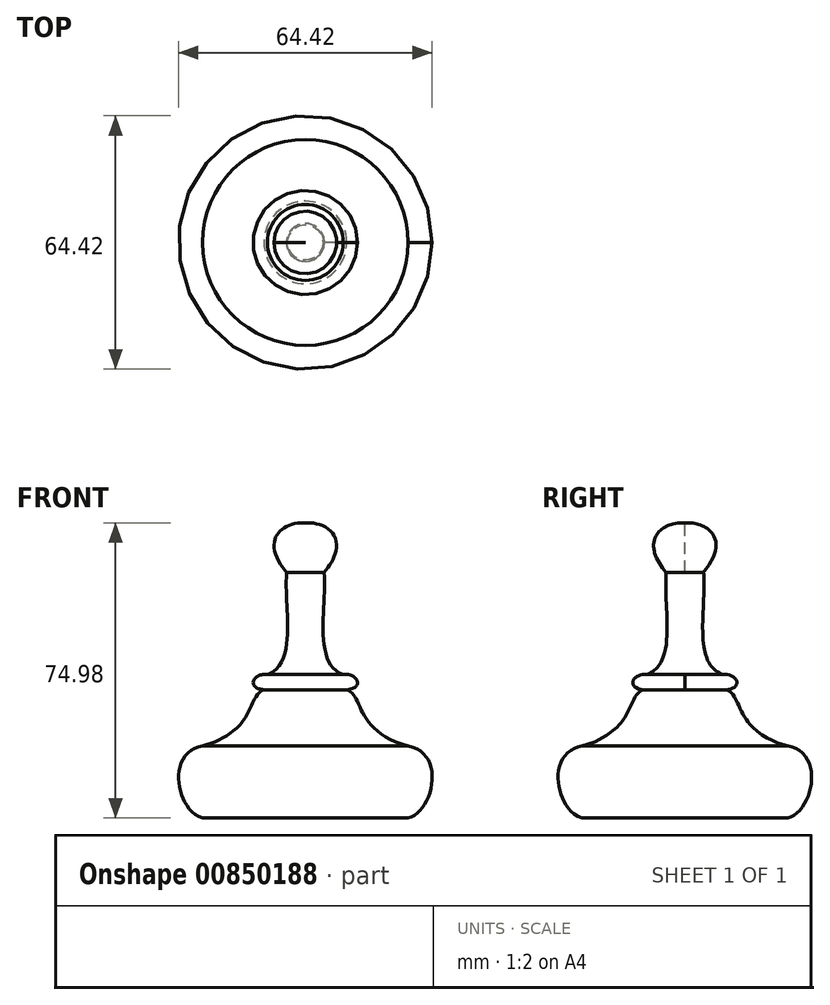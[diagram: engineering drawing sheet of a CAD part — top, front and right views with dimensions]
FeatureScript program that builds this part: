
annotation { "Feature Type Name" : "Feature", "Feature Type Description" : "" }
export const myFeature = defineFeature(function(context is Context, id is Id, definition is map)
    precondition{}
    {
        {
            var Q0;
            Q0=qCreatedBy(makeId("Front.planeOp"),FACE);
            var sketch = newSketch(context, id + "F0", { "sketchPlane" : qUnion([Q0])});
            skLineSegment(sketch, "E0", {"start": v(0, 0) * mm, "end": v(-26.14, 0) * mm});
            skFitSpline(sketch, "E1", {"points": [v(-26.14, 0) * mm, v(-26.14, 18.22) * mm], "startDerivative": vector(-19.1, 4.33) * mm, "endDerivative": vector(28.96, 4.76) * mm});
            skFitSpline(sketch, "E2", {"points": [v(-26.14, 18.22) * mm, v(-10.5, 32.53) * mm], "startDerivative": vector(41.24, 11.2) * mm, "endDerivative": vector(12.9, 3.47) * mm});
            skFitSpline(sketch, "E3", {"points": [v(-10.5, 32.53) * mm, v(-9.63, 36.43) * mm], "startDerivative": vector(-14.13, 1.41) * mm, "endDerivative": vector(10.63, -1.32) * mm});
            skFitSpline(sketch, "E4", {"points": [v(-9.63, 36.43) * mm, v(-4.77, 62.38) * mm], "startDerivative": vector(23.62, 7.74) * mm, "endDerivative": vector(2.22, 25.95) * mm});
            skFitSpline(sketch, "E5", {"points": [v(-4.77, 62.38) * mm, v(0, 74.97) * mm], "startDerivative": vector(-20.62, 24.13) * mm, "endDerivative": vector(18.38, -0.86) * mm});
            skLineSegment(sketch, "E6", {"start": v(0, 74.97) * mm, "end": v(0, 0) * mm});
            skSolve(sketch);
        }
        {
            var Q0;
            Q0 = qSketchRegion(id + "F0", true);
            var Q1;
            Q1=sQuery(id+"F0.wireOp",EDGE,"E6");
            revolve(context, id + "F1", {"surfaceOperationType" : NewSurfaceOperationType.NEW, "entities" : qUnion([Q0]), "axis" : qUnion([Q1]), "revolveType" : RevolveType.FULL});
        }
    });
